# Revit family: STL21912BR_27_30_STL21912PTO_27_30
name_source: partatom
category: Luminárias
units: mm (PartAtom-declared; Revit-internal decimal feet)

## family parameters
Com base no plano de trabalho = Não
Compartilhado = Não
Corte com vazios quando carregada = Não
Cota do conector redondo = Utilizar diâmetro
Fonte luminosa = Sim
Manter orientação da anotação = Não
Ponto de cálculo do ambiente = Não
Sempre na vertical = Sim
Tipo de parte = Normal

## types (4) — shared parameters
Altura = 0.03 m
Comprimento = 0.04 m
Cromado = Cromado
Dimerização = Não dimerizável
Fabricante = Stella
Filtro de cor = 16777215
Grau de proteção (IP) = IP20
IRC (Índice de reprodução de cores) = >90 (R9 >50)
Modelo = Mini Móbili
Potência = 2 W
Tensão Elétrica = 100V-240V
Troca de temperatura da cor de lâmpada com esmaecimento = <Nenhum>
URL = https://stella.com.br
Vidro = Vidro
Ângulo de Abertura = 25º
Ângulo de inclinação = 90.00°
zero-valued in all types: Elevação padrão

## per-type parameters (varying)
| type | Arquivo de rede fotométrica | Estrutura | Fluxo Luminoso | Logo Branco | Logo Preto | Luminoso | Referência | Temperatura da cor (K) |
| STL21912BR/27 - BIVOLT - 2700K - 140lm - 25° | STELLA - STL21912BR-27 - MINI MÓBILI QUADRADO 1,5W.ies | Al - Branco | 140 lm | Sim | Não | Luminoso - 2700K | STL21912BR/27 - BIVOLT | 2700 K |
| STL21912BR/30 - BIVOLT - 3000K - 150lm - 25° | STELLA - STL21912BR-30 - MINI MÓBILI QUADRADO 1,5W.ies | Al - Branco | 150 lm | Sim | Não | Luminoso - 3000K | STL21912BR/30 - BIVOLT | 3000 K |
| STL21912PTO/27 - BIVOLT - 2700K - 130lm - 25° | STELLA - STL21912PTO-27 - MINI MÓBILI QUADRADO 1,5W.ies | Al - Preto | 130 lm | Não | Sim | Luminoso - 2700K | STL21912PTO/27 - BIVOLT | 2700 K |
| STL21912PTO/30 - BIVOLT - 3000K - 140lm - 25° | STELLA - STL21912PTO-30 - MINI MÓBILI QUADRADO 1,5W.ies | Al - Preto | 140 lm | Não | Sim | Luminoso - 3000K | STL21912PTO/30 - BIVOLT | 3000 K |
